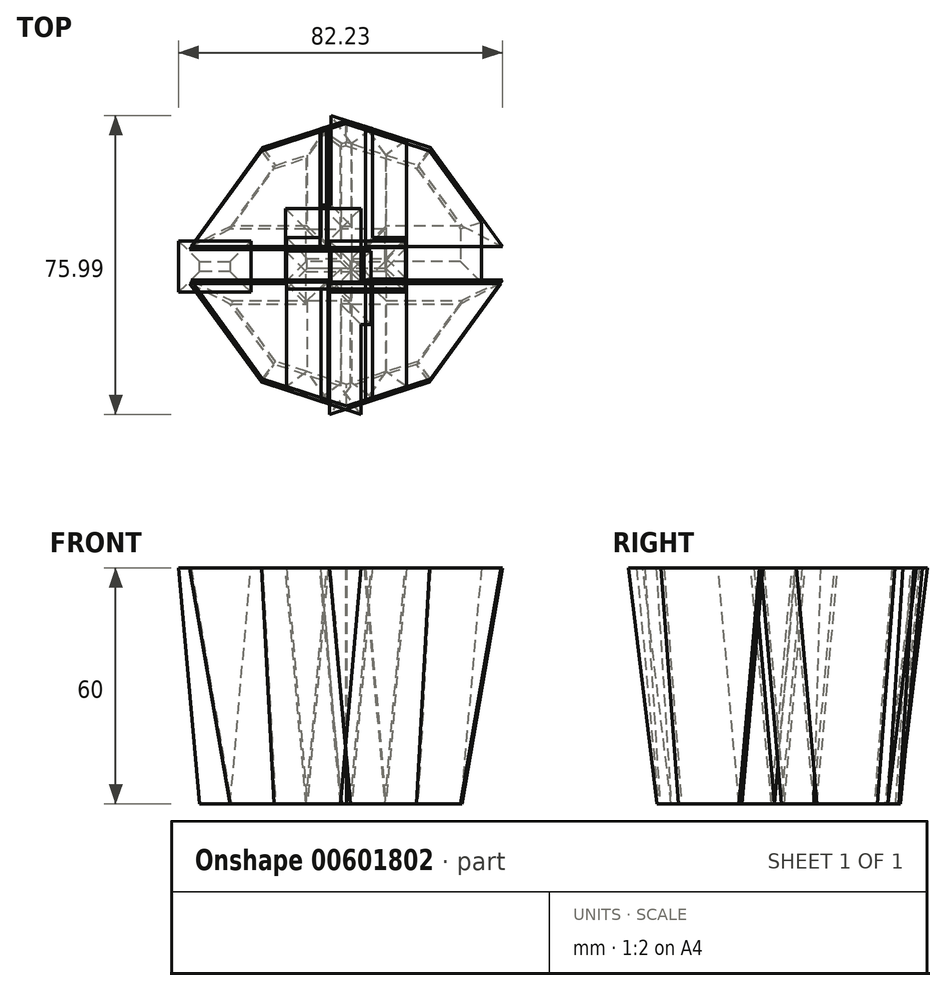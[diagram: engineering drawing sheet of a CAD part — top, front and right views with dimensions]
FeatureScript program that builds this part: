
annotation { "Feature Type Name" : "Feature", "Feature Type Description" : "" }
export const myFeature = defineFeature(function(context is Context, id is Id, definition is map)
    precondition{}
    {
        {
            var Q0;
            Q0=qCreatedBy(makeId("Top.planeOp"),FACE);
            var sketch = newSketch(context, id + "F0", { "sketchPlane" : qUnion([Q0])});
            skPoint(sketch, "E0.0", {"position": v(0, 30.78) * mm});
            skLineSegment(sketch, "E1.0", {"start": v(-0.3, 29.97) * mm, "end": v(17.8, 24.1) * mm});
            skLineSegment(sketch, "E1.1", {"start": v(17.8, 24.1) * mm, "end": v(28.98, 8.7) * mm});
            skLineSegment(sketch, "E1.2", {"start": v(28.98, 8.7) * mm, "end": v(28.98, -10.32) * mm});
            skLineSegment(sketch, "E1.3", {"start": v(28.98, -10.32) * mm, "end": v(17.8, -25.71) * mm});
            skLineSegment(sketch, "E1.4", {"start": v(17.8, -25.71) * mm, "end": v(-0.3, -31.59) * mm});
            skLineSegment(sketch, "E1.5", {"start": v(-0.3, -31.59) * mm, "end": v(-18.39, -25.71) * mm});
            skLineSegment(sketch, "E1.6", {"start": v(-18.39, -25.71) * mm, "end": v(-29.57, -10.32) * mm});
            skLineSegment(sketch, "E1.7", {"start": v(-29.57, -10.32) * mm, "end": v(-29.57, 8.7) * mm});
            skLineSegment(sketch, "E1.8", {"start": v(-29.57, 8.7) * mm, "end": v(-18.39, 24.1) * mm});
            skLineSegment(sketch, "E1.9", {"start": v(-18.39, 24.1) * mm, "end": v(-0.3, 29.97) * mm});
            skLineSegment(sketch, "E2", {"start": v(-0.3, 29.97) * mm, "end": v(-0.3, -31.59) * mm, "construction": true});
            skLineSegment(sketch, "E3", {"start": v(-29.57, -0.8) * mm, "end": v(28.98, -0.8) * mm, "construction": true});
            skLineSegment(sketch, "E4.bottom", {"start": v(-29.57, 8.7) * mm, "end": v(28.98, 8.7) * mm});
            skLineSegment(sketch, "E4.top", {"start": v(-29.57, -10.32) * mm, "end": v(28.98, -10.32) * mm});
            skLineSegment(sketch, "E4.left", {"start": v(-29.57, 8.7) * mm, "end": v(-29.57, -10.32) * mm});
            skLineSegment(sketch, "E5.bottom", {"start": v(9.7, 35.61) * mm, "end": v(-10.29, 35.61) * mm});
            skLineSegment(sketch, "E5.top", {"start": v(9.7, -37.23) * mm, "end": v(-10.29, -37.23) * mm});
            skLineSegment(sketch, "E5.left", {"start": v(9.7, 35.61) * mm, "end": v(9.7, -37.23) * mm});
            skLineSegment(sketch, "E5.right", {"start": v(-10.29, 35.61) * mm, "end": v(-10.29, -37.23) * mm});
            skPoint(sketch, "E5.middle", {"position": v(-0.3, -0.8) * mm});
            skLineSegment(sketch, "E6.bottom", {"start": v(36.82, 0.46) * mm, "end": v(-37.4, 0.46) * mm});
            skLineSegment(sketch, "E6.top", {"start": v(36.82, -2.08) * mm, "end": v(-37.4, -2.08) * mm});
            skLineSegment(sketch, "E6.left", {"start": v(36.82, 0.46) * mm, "end": v(36.82, -2.08) * mm});
            skLineSegment(sketch, "E6.right", {"start": v(-37.4, 0.46) * mm, "end": v(-37.4, -2.08) * mm});
            skLineSegment(sketch, "E7.bottom", {"start": v(0.98, 33.7) * mm, "end": v(-1.56, 33.7) * mm});
            skLineSegment(sketch, "E7.top", {"start": v(0.98, -35.32) * mm, "end": v(-1.56, -35.32) * mm});
            skLineSegment(sketch, "E7.left", {"start": v(0.98, 33.7) * mm, "end": v(0.98, -35.32) * mm});
            skLineSegment(sketch, "E7.right", {"start": v(-1.56, 33.7) * mm, "end": v(-1.56, -35.32) * mm});
            skPoint(sketch, "E8", {"position": v(9.7, 26.72) * mm});
            skLineSegment(sketch, "E9.MirrorCS", {"start": v(28.98, -0.8) * mm, "end": v(-29.57, -0.8) * mm, "construction": true});
            skSolve(sketch);
        }
        {
            var Q0;
            Q0=qCreatedBy(makeId("Top.planeOp"),FACE);
            var sketch = newSketch(context, id + "F1", { "sketchPlane" : qUnion([Q0])});
            skCircle(sketch, "E10.cCircle", {"center": v(0, 0) * mm, "radius": 30.78 * mm, "construction": true});
            skLineSegment(sketch, "E10.0", {"start": v(0, 30.78) * mm, "end": v(18.1, 24.9) * mm});
            skLineSegment(sketch, "E10.1", {"start": v(18.1, 24.9) * mm, "end": v(29.27, 9.51) * mm});
            skLineSegment(sketch, "E10.2", {"start": v(29.27, 9.51) * mm, "end": v(29.27, -9.51) * mm});
            skLineSegment(sketch, "E10.3", {"start": v(29.27, -9.51) * mm, "end": v(18.1, -24.9) * mm});
            skLineSegment(sketch, "E10.4", {"start": v(18.1, -24.9) * mm, "end": v(0, -30.78) * mm});
            skLineSegment(sketch, "E10.5", {"start": v(0, -30.78) * mm, "end": v(-18.1, -24.9) * mm});
            skLineSegment(sketch, "E10.6", {"start": v(-18.1, -24.9) * mm, "end": v(-29.27, -9.51) * mm});
            skLineSegment(sketch, "E10.7", {"start": v(-29.27, -9.51) * mm, "end": v(-29.27, 9.51) * mm});
            skLineSegment(sketch, "E10.8", {"start": v(-29.27, 9.51) * mm, "end": v(-18.1, 24.9) * mm});
            skLineSegment(sketch, "E10.9", {"start": v(-18.1, 24.9) * mm, "end": v(0, 30.78) * mm});
            skLineSegment(sketch, "E11", {"start": v(0, 30.78) * mm, "end": v(0, -30.78) * mm, "construction": true});
            skLineSegment(sketch, "E12", {"start": v(-29.27, 0) * mm, "end": v(29.27, 0) * mm, "construction": true});
            skLineSegment(sketch, "E13.bottom", {"start": v(-29.27, 9.51) * mm, "end": v(29.27, 9.51) * mm});
            skLineSegment(sketch, "E13.top", {"start": v(-29.27, -9.51) * mm, "end": v(29.27, -9.51) * mm});
            skLineSegment(sketch, "E13.left", {"start": v(-29.27, 9.51) * mm, "end": v(-29.27, -9.51) * mm});
            skLineSegment(sketch, "E14.bottom", {"start": v(10, 36.42) * mm, "end": v(-10, 36.42) * mm});
            skLineSegment(sketch, "E14.top", {"start": v(10, -36.42) * mm, "end": v(-10, -36.42) * mm});
            skLineSegment(sketch, "E14.left", {"start": v(10, 36.42) * mm, "end": v(10, -36.42) * mm});
            skLineSegment(sketch, "E14.right", {"start": v(-10, 36.42) * mm, "end": v(-10, -36.42) * mm});
            skLineSegment(sketch, "E15.bottom", {"start": v(37.1, 1.27) * mm, "end": v(-37.1, 1.27) * mm});
            skLineSegment(sketch, "E15.top", {"start": v(37.1, -1.27) * mm, "end": v(-37.1, -1.27) * mm});
            skLineSegment(sketch, "E15.left", {"start": v(37.1, 1.27) * mm, "end": v(37.1, -1.27) * mm});
            skLineSegment(sketch, "E15.right", {"start": v(-37.1, 1.27) * mm, "end": v(-37.1, -1.27) * mm});
            skLineSegment(sketch, "E16.bottom", {"start": v(1.27, 34.5) * mm, "end": v(-1.27, 34.5) * mm});
            skLineSegment(sketch, "E16.top", {"start": v(1.27, -34.5) * mm, "end": v(-1.27, -34.5) * mm});
            skLineSegment(sketch, "E16.left", {"start": v(1.27, 34.5) * mm, "end": v(1.27, -34.5) * mm});
            skLineSegment(sketch, "E16.right", {"start": v(-1.27, 34.5) * mm, "end": v(-1.27, -34.5) * mm});
            skPoint(sketch, "E17", {"position": v(10, 27.53) * mm});
            skLineSegment(sketch, "E18.MirrorCS", {"start": v(29.27, 0) * mm, "end": v(-29.27, 0) * mm, "construction": true});
            skSolve(sketch);
        }
        {
            var Q0;
            {var subQ0=sQuery(id+"F1.wireOp",EDGE,"E10.1");Q0=makeQuery(id+"F1.imprint","IMPRINT",FACE,{"disambiguationData":[TD([[makeQuery(id+"F1.imprint","IMPRINT",EDGE,{"derivedFrom":subQ0}),-1.0]])]});}
            var Q1;
            {var subQ0=sQuery(id+"F1.wireOp",EDGE,"E10.3");Q1=makeQuery(id+"F1.imprint","IMPRINT",FACE,{"disambiguationData":[TD([[makeQuery(id+"F1.imprint","IMPRINT",EDGE,{"derivedFrom":subQ0}),-1.0]])]});}
            var Q2;
            {var subQ0=sQuery(id+"F1.wireOp",EDGE,"E10.6");Q2=makeQuery(id+"F1.imprint","IMPRINT",FACE,{"disambiguationData":[TD([[makeQuery(id+"F1.imprint","IMPRINT",EDGE,{"derivedFrom":subQ0}),-1.0]])]});}
            var Q3;
            {var subQ0=sQuery(id+"F1.wireOp",EDGE,"E10.8");Q3=makeQuery(id+"F1.imprint","IMPRINT",FACE,{"disambiguationData":[TD([[makeQuery(id+"F1.imprint","IMPRINT",EDGE,{"derivedFrom":subQ0}),-1.0]])]});}
            var Q4;
            {var subQ0=sQuery(id+"F1.wireOp",EDGE,"E15.bottom");var subQ1=sQuery(id+"F1.wireOp",EDGE,"E13.left");var subQ2=makeQuery(id+"F1.imprint","INTERSECT",VERTEX,{"derivedFrom":[subQ1,subQ0]});Q4=makeQuery(id+"F1.imprint","IMPRINT",FACE,{"disambiguationData":[TD([[makeQuery(id+"F1.imprint","IMPRINT",EDGE,{"disambiguationData":[TD([[subQ2,-1.0]])],"derivedFrom":subQ1}),1.0]])]});}
            var Q5;
            {var subQ0=sQuery(id+"F1.wireOp",EDGE,"E15.bottom");var subQ1=sQuery(id+"F1.wireOp",EDGE,"E10.2");var subQ2=makeQuery(id+"F1.imprint","INTERSECT",VERTEX,{"derivedFrom":[subQ1,subQ0]});Q5=makeQuery(id+"F1.imprint","IMPRINT",FACE,{"disambiguationData":[TD([[makeQuery(id+"F1.imprint","IMPRINT",EDGE,{"disambiguationData":[TD([[subQ2,-1.0]])],"derivedFrom":subQ1}),-1.0]])]});}
            var Q6;
            {var subQ1=sQuery(id+"F1.wireOp",EDGE,"E10.4");var subQ7=sQuery(id+"F1.wireOp",EDGE,"E10.5");var subQ9=makeQuery(id+"F1.imprint","INTERSECT",VERTEX,{"derivedFrom":[subQ1,subQ7]});Q6=makeQuery(id+"F1.imprint","IMPRINT",FACE,{"disambiguationData":[TD([[makeQuery(id+"F1.imprint","IMPRINT",EDGE,{"disambiguationData":[TD([[subQ9,1.0]])],"derivedFrom":subQ1}),-1.0]])]});}
            var Q7;
            {var subQ1=sQuery(id+"F1.wireOp",EDGE,"E10.0");var subQ7=sQuery(id+"F1.wireOp",EDGE,"E10.9");var subQ8=makeQuery(id+"F1.imprint","INTERSECT",VERTEX,{"derivedFrom":[subQ1,subQ7]});Q7=makeQuery(id+"F1.imprint","IMPRINT",FACE,{"disambiguationData":[TD([[makeQuery(id+"F1.imprint","IMPRINT",EDGE,{"disambiguationData":[TD([[subQ8,-1.0]])],"derivedFrom":subQ1}),-1.0]])]});}
            var Q8;
            {var subQ0=sQuery(id+"F1.wireOp",EDGE,"E15.bottom");var subQ1=sQuery(id+"F1.wireOp",EDGE,"E14.left");var subQ2=makeQuery(id+"F1.imprint","INTERSECT",VERTEX,{"derivedFrom":[subQ1,subQ0]});Q8=makeQuery(id+"F1.imprint","IMPRINT",FACE,{"disambiguationData":[TD([[makeQuery(id+"F1.imprint","IMPRINT",EDGE,{"disambiguationData":[TD([[subQ2,-1.0]])],"derivedFrom":subQ1}),-1.0]])]});}
            var Q9;
            {var subQ0=sQuery(id+"F1.wireOp",EDGE,"E16.right");var subQ1=sQuery(id+"F1.wireOp",EDGE,"E13.bottom");var subQ2=makeQuery(id+"F1.imprint","INTERSECT",VERTEX,{"derivedFrom":[subQ1,subQ0]});Q9=makeQuery(id+"F1.imprint","IMPRINT",FACE,{"disambiguationData":[TD([[makeQuery(id+"F1.imprint","IMPRINT",EDGE,{"disambiguationData":[TD([[subQ2,-1.0]])],"derivedFrom":subQ1}),-1.0]])]});}
            var Q10;
            {var subQ0=sQuery(id+"F1.wireOp",EDGE,"E16.right");var subQ1=sQuery(id+"F1.wireOp",EDGE,"E13.top");var subQ2=makeQuery(id+"F1.imprint","INTERSECT",VERTEX,{"derivedFrom":[subQ1,subQ0]});Q10=makeQuery(id+"F1.imprint","IMPRINT",FACE,{"disambiguationData":[TD([[makeQuery(id+"F1.imprint","IMPRINT",EDGE,{"disambiguationData":[TD([[subQ2,-1.0]])],"derivedFrom":subQ1}),1.0]])]});}
            var Q11;
            {var subQ0=sQuery(id+"F1.wireOp",EDGE,"E15.bottom");var subQ1=sQuery(id+"F1.wireOp",EDGE,"E14.right");var subQ2=makeQuery(id+"F1.imprint","INTERSECT",VERTEX,{"derivedFrom":[subQ1,subQ0]});Q11=makeQuery(id+"F1.imprint","IMPRINT",FACE,{"disambiguationData":[TD([[makeQuery(id+"F1.imprint","IMPRINT",EDGE,{"disambiguationData":[TD([[subQ2,-1.0]])],"derivedFrom":subQ1}),1.0]])]});}
            var Q12;
            {var subQ0=sQuery(id+"F1.wireOp",EDGE,"E16.left");var subQ1=sQuery(id+"F1.wireOp",EDGE,"E15.bottom");var subQ2=makeQuery(id+"F1.imprint","INTERSECT",VERTEX,{"derivedFrom":[subQ1,subQ0]});Q12=makeQuery(id+"F1.imprint","IMPRINT",FACE,{"disambiguationData":[TD([[makeQuery(id+"F1.imprint","IMPRINT",EDGE,{"disambiguationData":[TD([[subQ2,-1.0]])],"derivedFrom":subQ1}),1.0]])]});}
            extrude(context, id + "F2", {"entities" : qUnion([Q0, Q1, Q2, Q3, Q4, Q5, Q6, Q7, Q8, Q9, Q10, Q11, Q12]), "depth" : 60 * mm, "offsetDistance" : 25.4 * mm, "hasDraft" : true, "draftAngle" : 5 * degree});
        }
        {
            var Q0;
            {var subQ5=sQuery(id+"F0.wireOp",EDGE,"E6.right");Q0=makeQuery(id+"F0.imprint","IMPRINT",FACE,{"disambiguationData":[TD([[makeQuery(id+"F0.imprint","IMPRINT",EDGE,{"derivedFrom":subQ5}),1.0]])]});}
            var Q1;
            {var subQ0=sQuery(id+"F0.wireOp",EDGE,"E1.1");Q1=makeQuery(id+"F0.imprint","IMPRINT",FACE,{"disambiguationData":[TD([[makeQuery(id+"F0.imprint","IMPRINT",EDGE,{"derivedFrom":subQ0}),-1.0]])]});}
            var Q2;
            {var subQ0=sQuery(id+"F0.wireOp",EDGE,"E1.3");Q2=makeQuery(id+"F0.imprint","IMPRINT",FACE,{"disambiguationData":[TD([[makeQuery(id+"F0.imprint","IMPRINT",EDGE,{"derivedFrom":subQ0}),-1.0]])]});}
            var Q3;
            {var subQ0=sQuery(id+"F0.wireOp",EDGE,"E1.6");Q3=makeQuery(id+"F0.imprint","IMPRINT",FACE,{"disambiguationData":[TD([[makeQuery(id+"F0.imprint","IMPRINT",EDGE,{"derivedFrom":subQ0}),-1.0]])]});}
            var Q4;
            {var subQ0=sQuery(id+"F0.wireOp",EDGE,"E1.8");Q4=makeQuery(id+"F0.imprint","IMPRINT",FACE,{"disambiguationData":[TD([[makeQuery(id+"F0.imprint","IMPRINT",EDGE,{"derivedFrom":subQ0}),-1.0]])]});}
            var Q5;
            {var subQ0=sQuery(id+"F0.wireOp",EDGE,"E5.left");var subQ1=sQuery(id+"F0.wireOp",EDGE,"E1.0");var subQ2=makeQuery(id+"F0.imprint","INTERSECT",VERTEX,{"derivedFrom":[subQ1,subQ0]});Q5=makeQuery(id+"F0.imprint","IMPRINT",FACE,{"disambiguationData":[TD([[makeQuery(id+"F0.imprint","IMPRINT",EDGE,{"disambiguationData":[TD([[subQ2,1.0]])],"derivedFrom":subQ1}),-1.0]])]});}
            var Q6;
            {var subQ0=sQuery(id+"F0.wireOp",EDGE,"E5.left");var subQ1=sQuery(id+"F0.wireOp",EDGE,"E1.4");var subQ2=makeQuery(id+"F0.imprint","INTERSECT",VERTEX,{"derivedFrom":[subQ1,subQ0]});Q6=makeQuery(id+"F0.imprint","IMPRINT",FACE,{"disambiguationData":[TD([[makeQuery(id+"F0.imprint","IMPRINT",EDGE,{"disambiguationData":[TD([[subQ2,-1.0]])],"derivedFrom":subQ1}),-1.0]])]});}
            var Q7;
            {var subQ0=sQuery(id+"F0.wireOp",EDGE,"E5.right");var subQ1=sQuery(id+"F0.wireOp",EDGE,"E1.5");var subQ2=makeQuery(id+"F0.imprint","INTERSECT",VERTEX,{"derivedFrom":[subQ1,subQ0]});Q7=makeQuery(id+"F0.imprint","IMPRINT",FACE,{"disambiguationData":[TD([[makeQuery(id+"F0.imprint","IMPRINT",EDGE,{"disambiguationData":[TD([[subQ2,1.0]])],"derivedFrom":subQ1}),-1.0]])]});}
            var Q8;
            {var subQ0=sQuery(id+"F0.wireOp",EDGE,"E6.bottom");var subQ1=sQuery(id+"F0.wireOp",EDGE,"E4.left");var subQ2=makeQuery(id+"F0.imprint","INTERSECT",VERTEX,{"derivedFrom":[subQ1,subQ0]});Q8=makeQuery(id+"F0.imprint","IMPRINT",FACE,{"disambiguationData":[TD([[makeQuery(id+"F0.imprint","IMPRINT",EDGE,{"disambiguationData":[TD([[subQ2,-1.0]])],"derivedFrom":subQ1}),1.0]])]});}
            var Q9;
            {var subQ0=sQuery(id+"F0.wireOp",EDGE,"E6.bottom");var subQ1=sQuery(id+"F0.wireOp",EDGE,"E1.2");var subQ2=makeQuery(id+"F0.imprint","INTERSECT",VERTEX,{"derivedFrom":[subQ1,subQ0]});Q9=makeQuery(id+"F0.imprint","IMPRINT",FACE,{"disambiguationData":[TD([[makeQuery(id+"F0.imprint","IMPRINT",EDGE,{"disambiguationData":[TD([[subQ2,-1.0]])],"derivedFrom":subQ1}),-1.0]])]});}
            var Q10;
            {var subQ1=sQuery(id+"F0.wireOp",EDGE,"E1.0");var subQ7=sQuery(id+"F0.wireOp",EDGE,"E1.9");var subQ8=makeQuery(id+"F0.imprint","INTERSECT",VERTEX,{"derivedFrom":[subQ1,subQ7]});Q10=makeQuery(id+"F0.imprint","IMPRINT",FACE,{"disambiguationData":[TD([[makeQuery(id+"F0.imprint","IMPRINT",EDGE,{"disambiguationData":[TD([[subQ8,-1.0]])],"derivedFrom":subQ1}),-1.0]])]});}
            var Q11;
            {var subQ0=sQuery(id+"F0.wireOp",EDGE,"E6.bottom");var subQ1=sQuery(id+"F0.wireOp",EDGE,"E5.left");var subQ2=makeQuery(id+"F0.imprint","INTERSECT",VERTEX,{"derivedFrom":[subQ1,subQ0]});Q11=makeQuery(id+"F0.imprint","IMPRINT",FACE,{"disambiguationData":[TD([[makeQuery(id+"F0.imprint","IMPRINT",EDGE,{"disambiguationData":[TD([[subQ2,-1.0]])],"derivedFrom":subQ1}),-1.0]])]});}
            var Q12;
            {var subQ0=sQuery(id+"F1.wireOp",EDGE,"E15.bottom");var subQ1=sQuery(id+"F1.wireOp",EDGE,"E14.right");var subQ2=makeQuery(id+"F1.imprint","INTERSECT",VERTEX,{"derivedFrom":[subQ1,subQ0]});Q12=makeQuery(id+"F1.imprint","IMPRINT",FACE,{"disambiguationData":[TD([[makeQuery(id+"F1.imprint","IMPRINT",EDGE,{"disambiguationData":[TD([[subQ2,-1.0]])],"derivedFrom":subQ1}),1.0]])]});}
            var Q13;
            {var subQ0=sQuery(id+"F0.wireOp",EDGE,"E5.right");var subQ1=sQuery(id+"F0.wireOp",EDGE,"E4.top");var subQ2=makeQuery(id+"F0.imprint","INTERSECT",VERTEX,{"derivedFrom":[subQ1,subQ0]});Q13=makeQuery(id+"F0.imprint","IMPRINT",FACE,{"disambiguationData":[TD([[makeQuery(id+"F0.imprint","IMPRINT",EDGE,{"disambiguationData":[TD([[subQ2,-1.0]])],"derivedFrom":subQ1}),1.0]])]});}
            var Q14;
            {var subQ0=sQuery(id+"F0.wireOp",EDGE,"E5.right");var subQ1=sQuery(id+"F0.wireOp",EDGE,"E4.bottom");var subQ2=makeQuery(id+"F0.imprint","INTERSECT",VERTEX,{"derivedFrom":[subQ1,subQ0]});Q14=makeQuery(id+"F0.imprint","IMPRINT",FACE,{"disambiguationData":[TD([[makeQuery(id+"F0.imprint","IMPRINT",EDGE,{"disambiguationData":[TD([[subQ2,-1.0]])],"derivedFrom":subQ1}),-1.0]])]});}
            var Q15;
            {var subQ1=sQuery(id+"F1.wireOp",EDGE,"E10.4");var subQ7=sQuery(id+"F1.wireOp",EDGE,"E10.5");var subQ9=makeQuery(id+"F1.imprint","INTERSECT",VERTEX,{"derivedFrom":[subQ1,subQ7]});Q15=makeQuery(id+"F1.imprint","IMPRINT",FACE,{"disambiguationData":[TD([[makeQuery(id+"F1.imprint","IMPRINT",EDGE,{"disambiguationData":[TD([[subQ9,1.0]])],"derivedFrom":subQ1}),-1.0]])]});}
            var Q16;
            {var subQ0=sQuery(id+"F0.wireOp",EDGE,"E7.right");var subQ1=sQuery(id+"F0.wireOp",EDGE,"E4.top");var subQ2=makeQuery(id+"F0.imprint","INTERSECT",VERTEX,{"derivedFrom":[subQ1,subQ0]});Q16=makeQuery(id+"F0.imprint","IMPRINT",FACE,{"disambiguationData":[TD([[makeQuery(id+"F0.imprint","IMPRINT",EDGE,{"disambiguationData":[TD([[subQ2,-1.0]])],"derivedFrom":subQ1}),1.0]])]});}
            var Q17;
            {var subQ0=sQuery(id+"F1.wireOp",EDGE,"E16.left");var subQ1=sQuery(id+"F1.wireOp",EDGE,"E15.bottom");var subQ2=makeQuery(id+"F1.imprint","INTERSECT",VERTEX,{"derivedFrom":[subQ1,subQ0]});Q17=makeQuery(id+"F1.imprint","IMPRINT",FACE,{"disambiguationData":[TD([[makeQuery(id+"F1.imprint","IMPRINT",EDGE,{"disambiguationData":[TD([[subQ2,-1.0]])],"derivedFrom":subQ1}),1.0]])]});}
            var Q18;
            {var subQ0=sQuery(id+"F1.wireOp",EDGE,"E16.right");var subQ1=sQuery(id+"F1.wireOp",EDGE,"E13.bottom");var subQ2=makeQuery(id+"F1.imprint","INTERSECT",VERTEX,{"derivedFrom":[subQ1,subQ0]});Q18=makeQuery(id+"F1.imprint","IMPRINT",FACE,{"disambiguationData":[TD([[makeQuery(id+"F1.imprint","IMPRINT",EDGE,{"disambiguationData":[TD([[subQ2,-1.0]])],"derivedFrom":subQ1}),-1.0]])]});}
            var Q19;
            {var subQ0=sQuery(id+"F1.wireOp",EDGE,"E14.left");var subQ1=sQuery(id+"F1.wireOp",EDGE,"E10.0");var subQ2=makeQuery(id+"F1.imprint","INTERSECT",VERTEX,{"derivedFrom":[subQ1,subQ0]});Q19=makeQuery(id+"F1.imprint","IMPRINT",FACE,{"disambiguationData":[TD([[makeQuery(id+"F1.imprint","IMPRINT",EDGE,{"disambiguationData":[TD([[subQ2,1.0]])],"derivedFrom":subQ1}),-1.0]])]});}
            var Q20;
            {var subQ0=sQuery(id+"F1.wireOp",EDGE,"E16.left");var subQ1=sQuery(id+"F1.wireOp",EDGE,"E13.top");var subQ2=makeQuery(id+"F1.imprint","INTERSECT",VERTEX,{"derivedFrom":[subQ1,subQ0]});Q20=makeQuery(id+"F1.imprint","IMPRINT",FACE,{"disambiguationData":[TD([[makeQuery(id+"F1.imprint","IMPRINT",EDGE,{"disambiguationData":[TD([[subQ2,-1.0]])],"derivedFrom":subQ1}),1.0]])]});}
            var Q21;
            {var subQ0=sQuery(id+"F1.wireOp",EDGE,"E14.left");var subQ1=sQuery(id+"F1.wireOp",EDGE,"E10.4");var subQ2=makeQuery(id+"F1.imprint","INTERSECT",VERTEX,{"derivedFrom":[subQ1,subQ0]});Q21=makeQuery(id+"F1.imprint","IMPRINT",FACE,{"disambiguationData":[TD([[makeQuery(id+"F1.imprint","IMPRINT",EDGE,{"disambiguationData":[TD([[subQ2,-1.0]])],"derivedFrom":subQ1}),-1.0]])]});}
            var Q22;
            {var subQ0=sQuery(id+"F1.wireOp",EDGE,"E14.right");var subQ1=sQuery(id+"F1.wireOp",EDGE,"E10.5");var subQ2=makeQuery(id+"F1.imprint","INTERSECT",VERTEX,{"derivedFrom":[subQ1,subQ0]});Q22=makeQuery(id+"F1.imprint","IMPRINT",FACE,{"disambiguationData":[TD([[makeQuery(id+"F1.imprint","IMPRINT",EDGE,{"disambiguationData":[TD([[subQ2,1.0]])],"derivedFrom":subQ1}),-1.0]])]});}
            var Q23;
            {var subQ0=sQuery(id+"F1.wireOp",EDGE,"E16.left");var subQ1=sQuery(id+"F1.wireOp",EDGE,"E13.bottom");var subQ2=makeQuery(id+"F1.imprint","INTERSECT",VERTEX,{"derivedFrom":[subQ1,subQ0]});Q23=makeQuery(id+"F1.imprint","IMPRINT",FACE,{"disambiguationData":[TD([[makeQuery(id+"F1.imprint","IMPRINT",EDGE,{"disambiguationData":[TD([[subQ2,-1.0]])],"derivedFrom":subQ1}),-1.0]])]});}
            var Q24;
            {var subQ1=sQuery(id+"F0.wireOp",EDGE,"E4.bottom");var subQ3=sQuery(id+"F0.wireOp",EDGE,"E5.left");var subQ4=makeQuery(id+"F0.imprint","INTERSECT",VERTEX,{"derivedFrom":[subQ1,subQ3]});Q24=makeQuery(id+"F0.imprint","IMPRINT",FACE,{"disambiguationData":[TD([[makeQuery(id+"F0.imprint","IMPRINT",EDGE,{"disambiguationData":[TD([[subQ4,-1.0]])],"derivedFrom":subQ3}),1.0]])]});}
            extrude(context, id + "F3", {"entities" : qUnion([Q0, Q1, Q2, Q3, Q4, Q5, Q6, Q7, Q8, Q9, Q10, Q11, Q12, Q13, Q14, Q15, Q16, Q17, Q18, Q19, Q20, Q21, Q22, Q23, Q24]), "depth" : 60 * mm, "offsetDistance" : 25.4 * mm, "hasDraft" : true, "draftAngle" : 5 * degree});
        }
    });
